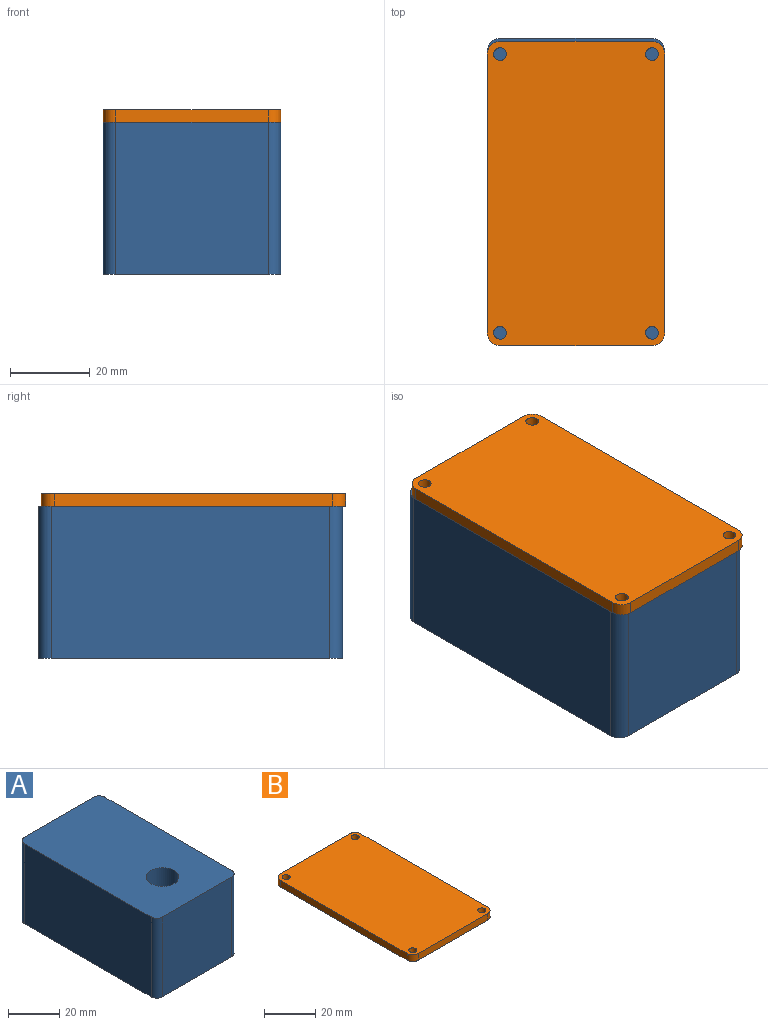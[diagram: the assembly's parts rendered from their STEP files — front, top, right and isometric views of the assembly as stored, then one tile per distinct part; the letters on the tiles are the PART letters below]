
ASSEMBLY  parts=2 mates=1
PART A: 11 faces, bbox 44.5x76.2x38.1 mm
  f0: plane 69.85x38.1mm, normal (1,0,0), area 2661.3mm2, adj f1,f7,f8,f9
  f1: cylinder r=3.17mm len=38.1mm, axis (0,0,-1), area 190mm2, adj f0,f2,f8,f9
  f2: plane 38.1x38.1mm, normal (0,1,0), area 1451.6mm2, adj f1,f3,f8,f9
  f3: cylinder r=3.17mm len=38.1mm, axis (0,0,-1), area 190mm2, adj f2,f4,f8,f9
  f4: plane 69.85x38.1mm, normal (-1,0,0), area 2661.3mm2, adj f3,f5,f8,f9
  f5: cylinder r=3.17mm len=38.1mm, axis (0,0,-1), area 190mm2, adj f4,f6,f8,f9
  f6: plane 38.1x38.1mm, normal (0,-1,0), area 1451.6mm2, adj f5,f7,f8,f9
  f7: cylinder r=3.17mm len=38.1mm, axis (0,0,-1), area 190mm2, adj f0,f6,f8,f9
  f8: plane 76.2x44.45mm, normal (0,0,1), area 3251.8mm2, adj f0,f1,f2,f3,f4,f5,f6,f7
  f9: plane 76.2x44.45mm, normal (0,0,-1), area 3251.8mm2, adj f0,f1,f2,f3,f4,f5,f6,f7
  f10: cylinder r=6.35mm len=38.1mm, axis (0,0,1), area 1520.1mm2, adj f8,f9
PART B: 14 faces, bbox 44.5x76.2x3.2 mm
  f0: plane 69.85x3.18mm, normal (1,0,0), area 221.8mm2, adj f1,f7,f8,f9
  f1: cylinder r=3.17mm len=3.18mm, axis (0,0,-1), area 15.8mm2, adj f0,f2,f8,f9
  f2: plane 38.1x3.18mm, normal (0,1,0), area 121mm2, adj f1,f3,f8,f9
  f3: cylinder r=3.17mm len=3.18mm, axis (0,0,-1), area 15.8mm2, adj f2,f4,f8,f9
  f4: plane 69.85x3.18mm, normal (-1,0,0), area 221.8mm2, adj f3,f5,f8,f9
  f5: cylinder r=3.17mm len=3.18mm, axis (0,0,-1), area 15.8mm2, adj f4,f6,f8,f9
  f6: plane 38.1x3.18mm, normal (0,-1,0), area 121mm2, adj f5,f7,f8,f9
  f7: cylinder r=3.17mm len=3.18mm, axis (0,0,-1), area 15.8mm2, adj f0,f6,f8,f9
  f8: plane 76.2x44.45mm, normal (0,0,1), area 3346.8mm2, adj f0,f1,f2,f3,f4,f5,f6,f7
  f9: plane 76.2x44.45mm, normal (0,0,-1), area 3346.8mm2, adj f0,f1,f2,f3,f4,f5,f6,f7
  f10: cylinder r=1.59mm len=3.18mm, axis (0,0,1), area 31.7mm2, adj f8,f9
  f11: cylinder r=1.59mm len=3.18mm, axis (0,0,1), area 31.7mm2, adj f8,f9
  f12: cylinder r=1.59mm len=3.18mm, axis (0,0,1), area 31.7mm2, adj f8,f9
  f13: cylinder r=1.59mm len=3.18mm, axis (0,0,1), area 31.7mm2, adj f8,f9
PLACE A rot(axis=(1,0,0),180deg) t=(0,0.74,0)mm
PLACE B at identity fixed
MATE fastened A.f9 <-> B.f9  axis (0,0,1) through (0,0,0)mm
